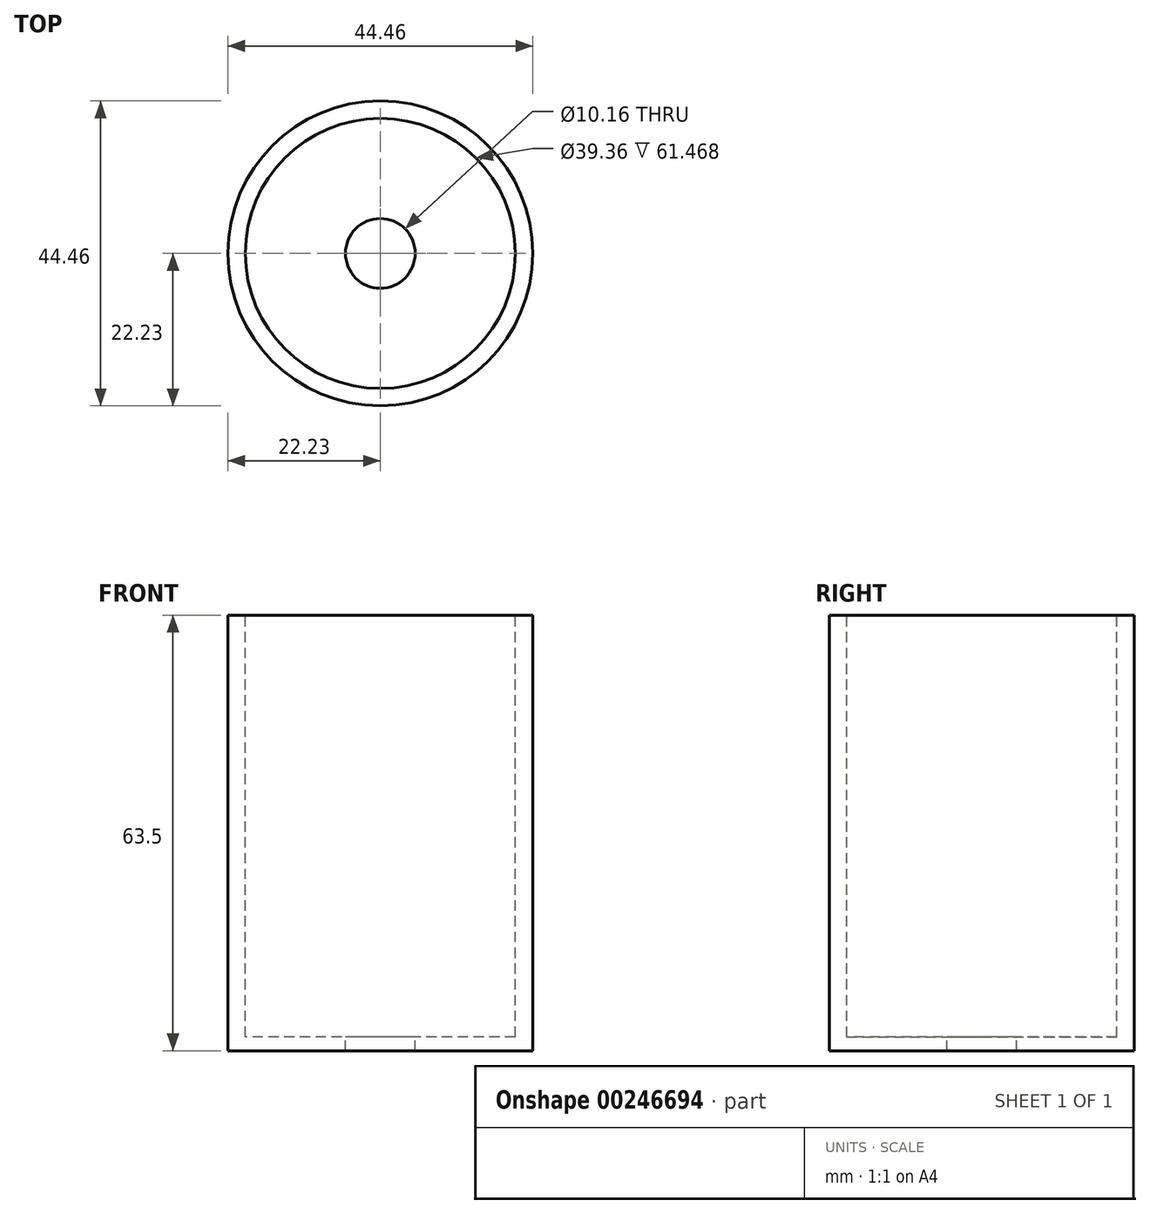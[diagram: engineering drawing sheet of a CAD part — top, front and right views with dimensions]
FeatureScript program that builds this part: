
annotation { "Feature Type Name" : "Feature", "Feature Type Description" : "" }
export const myFeature = defineFeature(function(context is Context, id is Id, definition is map)
    precondition{}
    {
        {
            var Q0;
            Q0=qCreatedBy(makeId("Front.planeOp"),FACE);
            var sketch = newSketch(context, id + "F0", { "sketchPlane" : qUnion([Q0])});
            skLineSegment(sketch, "E0.bottom", {"start": v(-22.22, 31.75) * mm, "end": v(22.23, 31.75) * mm});
            skLineSegment(sketch, "E0.top", {"start": v(-22.23, -31.75) * mm, "end": v(22.22, -31.75) * mm});
            skLineSegment(sketch, "E0.left", {"start": v(-22.22, 31.75) * mm, "end": v(-22.23, -31.75) * mm});
            skLineSegment(sketch, "E0.right", {"start": v(22.23, 31.75) * mm, "end": v(22.22, -31.75) * mm});
            skPoint(sketch, "E0.middle", {"position": v(0, 0) * mm});
            skLineSegment(sketch, "E1", {"start": v(0, 31.75) * mm, "end": v(0, -31.75) * mm});
            skSolve(sketch);
        }
        {
            var Q0;
            {var subQ0=sQuery(id+"F0.wireOp",EDGE,"E0.left");Q0=makeQuery(id+"F0.imprint","IMPRINT",FACE,{"disambiguationData":[TD([[makeQuery(id+"F0.imprint","IMPRINT",EDGE,{"derivedFrom":subQ0}),1.0]])]});}
            var Q1;
            Q1=sQuery(id+"F0.wireOp",EDGE,"E1");
            revolve(context, id + "F1", {"entities" : qUnion([Q0]), "axis" : qUnion([Q1]), "revolveType" : RevolveType.FULL});
        }
        {
            var Q0;
            Q0=makeQuery(id+"F1.opRevolve","SWEPT_FACE",FACE,{"disambiguationData":[OSD([sQuery(id+"F0.wireOp",EDGE,"E0.bottom")])]});
            var sketch = newSketch(context, id + "F2", { "sketchPlane" : qUnion([Q0])});
            skPoint(sketch, "E2", {"position": v(0, 0) * mm});
            skCircle(sketch, "E3", {"center": v(0, 0) * mm, "radius": 19.68 * mm});
            skSolve(sketch);
        }
        {
            var Q0;
            Q0=sQuery(id+"F2.wireOp",VERTEX,"E2");
            var Q1;
            Q1=makeQuery(id+"F1.opRevolve","SWEPT_BODY",BODY,{"disambiguationData":[OSD([sQuery(id+"F0.wireOp",EDGE,"E0.bottom"),sQuery(id+"F0.wireOp",EDGE,"E0.top"),sQuery(id+"F0.wireOp",EDGE,"E0.left"),sQuery(id+"F0.wireOp",EDGE,"E1")])]});
            hole(context, id + "F3", {"style" : HoleStyle.SIMPLE, "endStyle" : HoleEndStyle.THROUGH, "holeDiameter" : 10.16 * mm, "tappedDepth" : 12.7 * mm, "tapClearance" : 3, "locations" : qUnion([Q0]), "scope" : qUnion([Q1])});
        }
        {
            var Q0;
            Q0=makeQuery(id+"F2.imprint","IMPRINT",FACE,{"disambiguationData":[TD([[makeQuery(id+"F2.imprint","IMPRINT",EDGE,{"derivedFrom":sQuery(id+"F2.wireOp",EDGE,"E3")}),1.0]])]});
            extrude(context, id + "F4", {"entities" : qUnion([Q0]), "operationType" : NewBodyOperationType.REMOVE, "oppositeDirection" : true, "depth" : 61.47 * mm});
        }
    });
